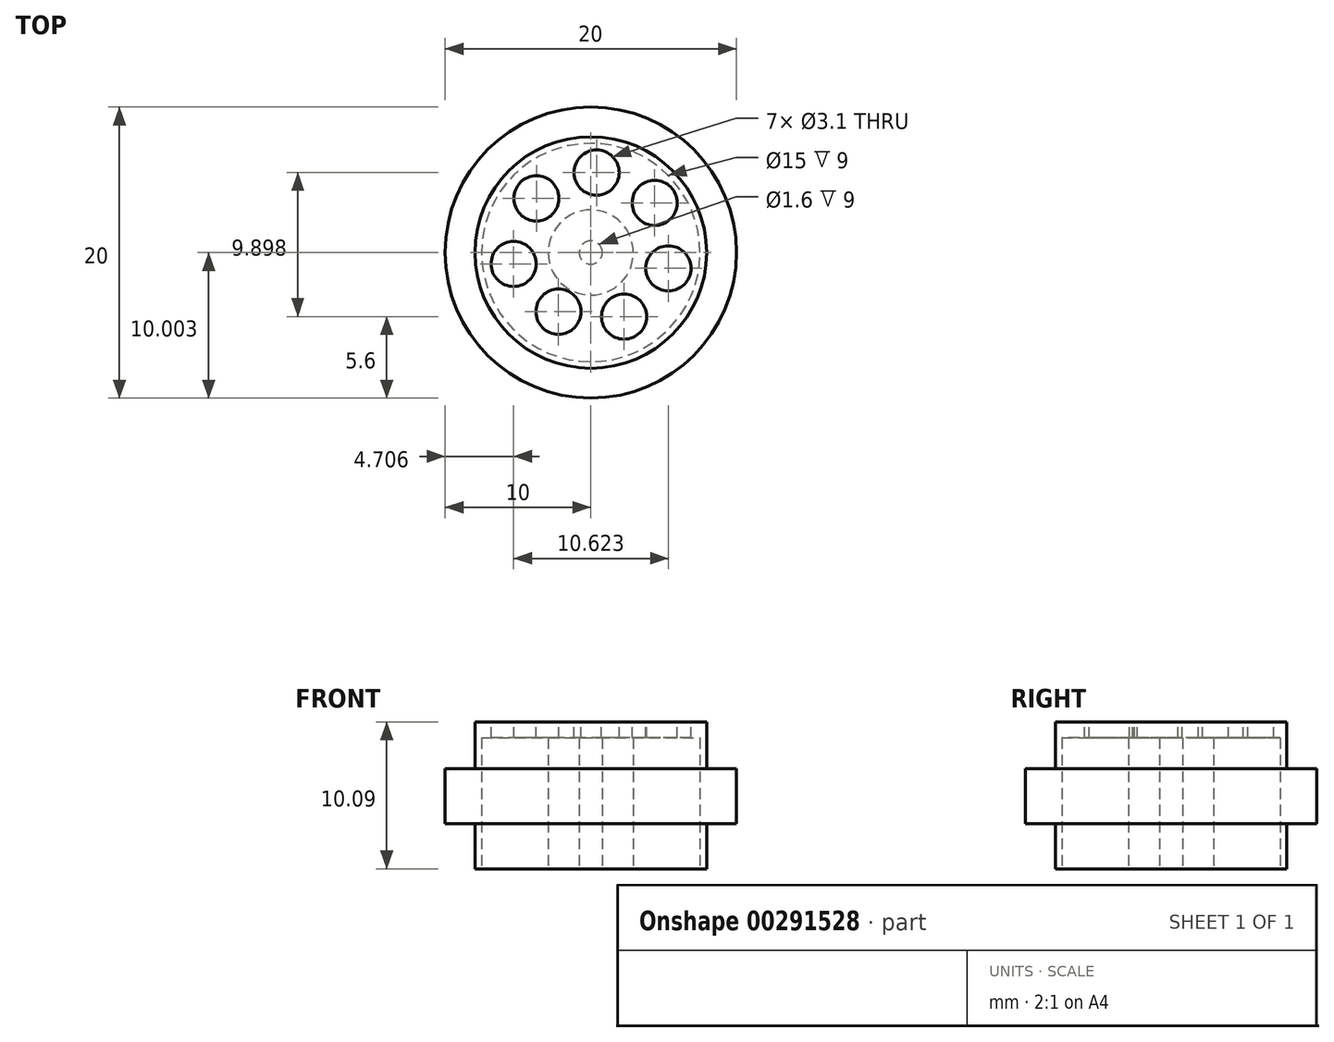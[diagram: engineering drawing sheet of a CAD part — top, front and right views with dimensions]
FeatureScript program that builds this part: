
annotation { "Feature Type Name" : "Feature", "Feature Type Description" : "" }
export const myFeature = defineFeature(function(context is Context, id is Id, definition is map)
    precondition{}
    {
        {
            var Q0;
            Q0=qCreatedBy(makeId("Top.planeOp"),FACE);
            var sketch = newSketch(context, id + "F0", { "sketchPlane" : qUnion([Q0])});
            skCircle(sketch, "E0", {"center": v(-16.16, 42.17) * mm, "radius": 7.95 * mm});
            skSolve(sketch);
        }
        {
            var Q0;
            Q0 = qSketchRegion(id + "F0", true);
            extrude(context, id + "F1", {"entities" : qUnion([Q0]), "depth" : 3.1 * mm});
        }
        {
            var Q0;
            Q0=makeQuery(id+"F1.opExtrude","CAP_FACE",FACE,{"disambiguationData":[OSD([sQuery(id+"F0.wireOp",EDGE,"E0")])],"isStart":false});
            var sketch = newSketch(context, id + "F2", { "sketchPlane" : qUnion([Q0])});
            skCircle(sketch, "E1", {"center": v(-16.16, 42.17) * mm, "radius": 10 * mm});
            skSolve(sketch);
        }
        {
            var Q0;
            Q0 = qSketchRegion(id + "F2", true);
            extrude(context, id + "F3", {"entities" : qUnion([Q0]), "operationType" : NewBodyOperationType.ADD, "depth" : 3.77 * mm});
        }
        {
            var Q0;
            Q0=makeQuery(id+"F3.opExtrude","CAP_FACE",FACE,{"disambiguationData":[OSD([sQuery(id+"F2.wireOp",EDGE,"E1")])],"isStart":false});
            var sketch = newSketch(context, id + "F4", { "sketchPlane" : qUnion([Q0])});
            skCircle(sketch, "E2", {"center": v(-16.16, 42.17) * mm, "radius": 7.95 * mm});
            skSolve(sketch);
        }
        {
            var Q0;
            Q0 = qSketchRegion(id + "F4", true);
            extrude(context, id + "F5", {"entities" : qUnion([Q0]), "operationType" : NewBodyOperationType.ADD, "depth" : 3.22 * mm});
        }
        {
            var Q0;
            Q0=makeQuery(id+"F5.opExtrude","CAP_FACE",FACE,{"disambiguationData":[OSD([sQuery(id+"F4.wireOp",EDGE,"E2")])],"isStart":false});
            var sketch = newSketch(context, id + "F6", { "sketchPlane" : qUnion([Q0])});
            skCircle(sketch, "E3", {"center": v(-15.76, 47.67) * mm, "radius": 1.55 * mm});
            skCircle(sketch, "E4", {"center": v(-19.9, 45.9) * mm, "radius": 1.55 * mm});
            skCircle(sketch, "E5", {"center": v(-21.45, 41.4) * mm, "radius": 1.55 * mm});
            skCircle(sketch, "E6", {"center": v(-18.38, 38.11) * mm, "radius": 1.55 * mm});
            skCircle(sketch, "E7", {"center": v(-13.88, 37.77) * mm, "radius": 1.55 * mm});
            skCircle(sketch, "E8", {"center": v(-10.83, 41.08) * mm, "radius": 1.55 * mm});
            skCircle(sketch, "E9", {"center": v(-11.77, 45.58) * mm, "radius": 1.55 * mm});
            skSolve(sketch);
        }
        {
            var Q0;
            Q0 = qSketchRegion(id + "F6", true);
            extrude(context, id + "F7", {"entities" : qUnion([Q0]), "operationType" : NewBodyOperationType.REMOVE, "oppositeDirection" : true, "depth" : 25 * mm});
        }
        {
            var Q0;
            Q0=makeQuery(id+"F1.opExtrude","CAP_FACE",FACE,{"disambiguationData":[OSD([sQuery(id+"F0.wireOp",EDGE,"E0")])],"isStart":true});
            var sketch = newSketch(context, id + "F8", { "sketchPlane" : qUnion([Q0])});
            skCircle(sketch, "E10", {"center": v(-16.16, -42.17) * mm, "radius": 7.5 * mm});
            skCircle(sketch, "E11", {"center": v(-16.16, -42.17) * mm, "radius": 2.93 * mm});
            skCircle(sketch, "E12", {"center": v(-16.16, -42.17) * mm, "radius": 0.8 * mm});
            skSolve(sketch);
        }
        {
            var Q0;
            Q0=makeQuery(id+"F8.imprint","IMPRINT",FACE,{"disambiguationData":[TD([[makeQuery(id+"F8.imprint","IMPRINT",EDGE,{"derivedFrom":sQuery(id+"F8.wireOp",EDGE,"E12")}),1.0]])]});
            var Q1;
            Q1=makeQuery(id+"F8.imprint","IMPRINT",FACE,{"disambiguationData":[TD([[makeQuery(id+"F8.imprint","IMPRINT",EDGE,{"derivedFrom":sQuery(id+"F8.wireOp",EDGE,"E10")}),1.0]])]});
            extrude(context, id + "F9", {"entities" : qUnion([Q0, Q1]), "operationType" : NewBodyOperationType.REMOVE, "oppositeDirection" : true, "depth" : 9 * mm});
        }
    });
